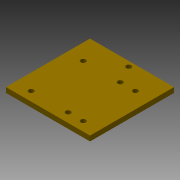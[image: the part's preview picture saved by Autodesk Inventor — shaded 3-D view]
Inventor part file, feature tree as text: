
AUTODESK INVENTOR PART (.ipt)
format: ipt  version: 2013 SP2 (Build 170200200, 200)  size: 106,496 bytes
history: native  units: mm
features: extrude x2, sketch x1
ambient origin geometry x8: Origin, YZ Plane, XZ Plane, XY Plane, X Axis, Y Axis, Z Axis, Center Point
bodies: Solid1 (feature_tree)
feature tree (3):
  extrude  "Extrusion1"  Depth=3.0mm
  extrude  "Extrusion2"  Depth=50.0mm TaperAngle=0.0deg
  sketch  "Sketch1"  dims[d0=50.0mm d1=3.0mm d2=50.0mm d3=0.0mm d10=10.0mm d11=0.0mm d12=31.0mm d13=31.0mm d15=3.0mm d16=3.0mm d17=3.0mm d18=3.0mm d19=3.0mm d21=3.0mm d22=3.0mm d23=20.0mm d24=3.0mm d26=5.5mm d27=26.0mm d28=3.0mm d29=3.0mm d31=3.0mm d32=3.0mm d33=9.0mm]
